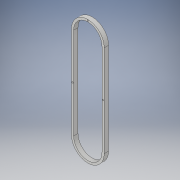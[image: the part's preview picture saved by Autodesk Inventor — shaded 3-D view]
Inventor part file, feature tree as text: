
AUTODESK INVENTOR PART (.ipt)
format: ipt  version: 2018 (Build 220112000, 112)  size: 128,000 bytes
history: native  units: in
note: dims shown in document units (in); Inventor stores cm internally (conversion verified against a paired STEP export)
features: sketch x4, hole x3, extrude x1
ambient origin geometry x8: Origin, YZ Plane, XZ Plane, XY Plane, X Axis, Y Axis, Z Axis, Center Point
bodies: Solid1 (feature_tree)
feature tree (8):
  extrude  "Extrusion1"  TaperAngle=90.0deg  [1 undecoded]
  hole  "Hole1"  [1 undecoded]
  hole  "Hole3"  [1 undecoded]
  hole  "Hole4"  [1 undecoded]
  sketch  "Sketch1"  dims[d0=8.2677in d1=90.0deg]
  sketch  "Sketch3"  dims[d2=8.2677in d3=90.0deg]
  sketch  "Sketch5"  dims[d4=8.2677in d5=90.0deg]
  sketch  "Sketch6"  dims[d6=8.2677in d7=90.0deg d8=0.3937in d9=0.0in d11=0.1181in d12=0.1181in d13=0.1181in d14=0.1181in d15=0.2953in d16=0.1476in d17=0.0984in d18=90.0deg d19=0.3937in d20=0.8108in d31=0.1181in d32=0.1181in d33=0.2953in d34=0.1476in d35=0.0984in d36=90.0deg d37=0.3937in d38=0.8108in d39=0.1181in d40=0.1181in d41=0.2953in d42=0.1476in d43=0.0984in d44=90.0deg d45=0.3937in d46=0.8108in]
note: 4 required parameter values undecoded (feature->parameter linkage not recoverable at this tier; creation-order binding heuristic only, values carry confidence <= 0.55)
